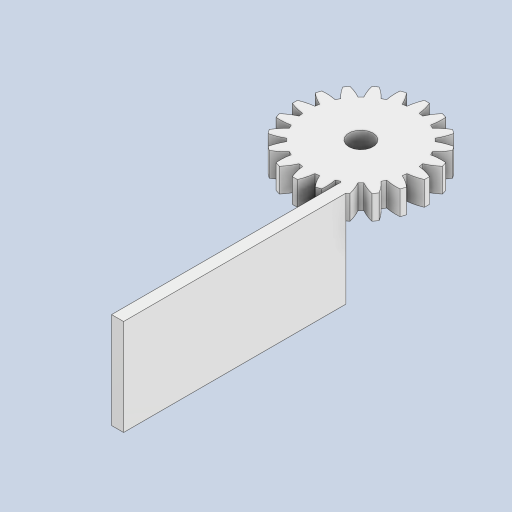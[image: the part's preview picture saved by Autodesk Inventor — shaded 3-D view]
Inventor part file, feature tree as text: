
AUTODESK INVENTOR PART (.ipt)
format: ipt  version: 2023 (Build 270158000, 158)  size: 244,736 bytes
history: native  units: mm (DEFAULTED — no unit token found)
features: sketch x5, extrude x4, plane x3, other x3
ambient origin geometry x8: Origin, YZ Plane, XZ Plane, XY Plane, X Axis, Y Axis, Z Axis, Center Point
bodies: Solid1 (feature_tree)
feature tree (15):
  extrude  "Extrusion1"  Depth=10.0mm TaperAngle=0.0deg
  plane  "Work Plane2"
  plane  "Work Plane8"
  plane  "Work Plane9"
  other  "平歯車"
  extrude  "押し出し2"  Depth=10.0mm TaperAngle=0.0deg
  extrude  "押し出し3"  Depth=40.0mm
  extrude  "押し出し4"  Depth=40.0mm TaperAngle=0.0deg
  sketch  "Sketch1"  dims[d0=55.0mm d1=10.0mm d2=0.0mm]
  sketch  "Sketch2"  dims[d3=50.0mm d4=10.0mm d5=0.0mm d16=50.0mm d17=0.0mm d34=1.570796mm d39=0.0mm d41=0.0mm d43=50.0mm d46=50.0mm d47=0.0mm d48=0.0mm d49=10.0mm d50=8.0mm d51=0.0mm d52=5.1mm d53=2.0mm d54=0.0mm d55=100.0mm d56=5.0mm d57=40.0mm d58=0.0mm]
  other  "Srf1"
  sketch  "スケッチ3"
  sketch  "スケッチ4"
  sketch  "スケッチ5"
  other  "ピッチ円直径"
